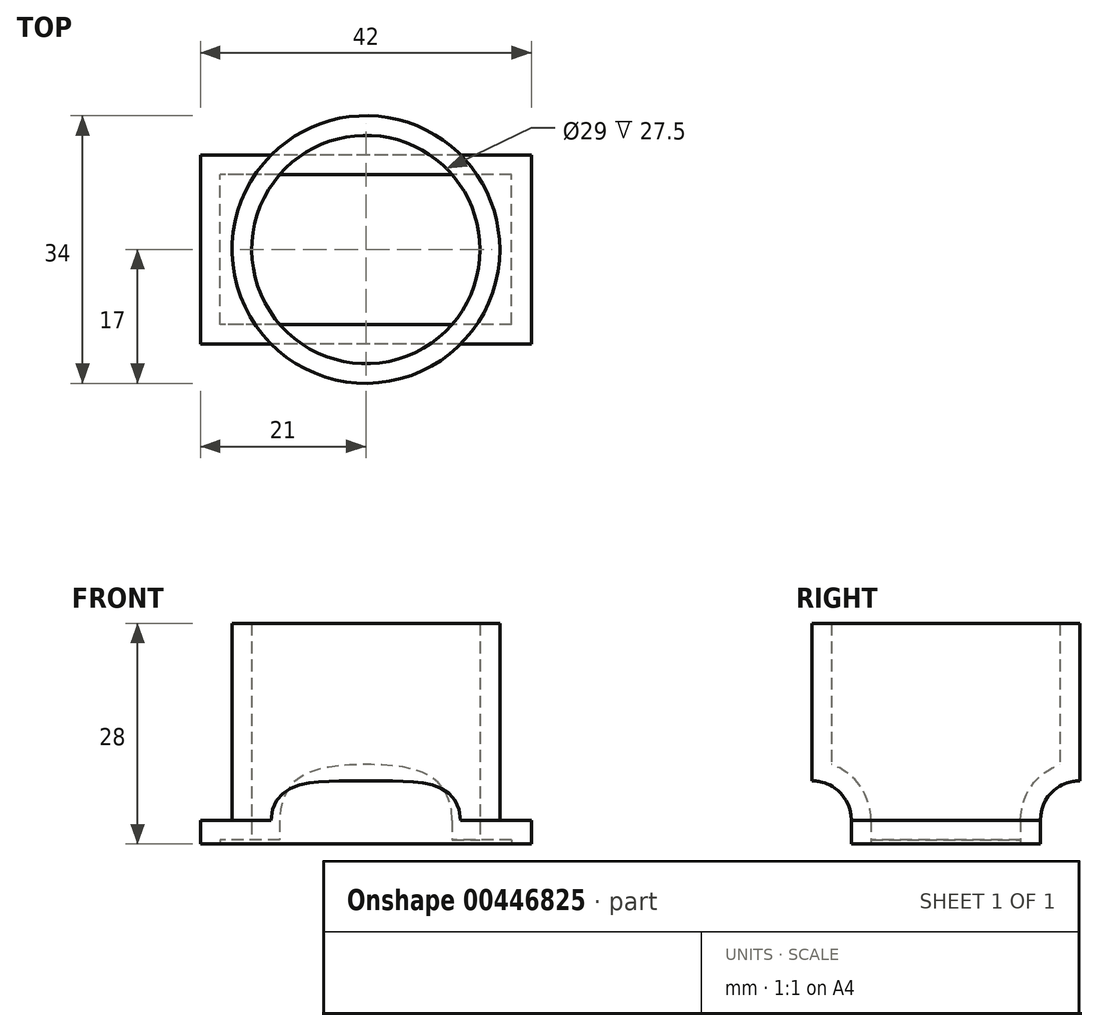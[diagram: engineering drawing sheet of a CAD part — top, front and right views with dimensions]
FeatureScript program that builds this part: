
annotation { "Feature Type Name" : "Feature", "Feature Type Description" : "" }
export const myFeature = defineFeature(function(context is Context, id is Id, definition is map)
    precondition{}
    {
        {
            var Q0;
            Q0=qCreatedBy(makeId("Top.planeOp"),FACE);
            var sketch = newSketch(context, id + "F0", { "sketchPlane" : qUnion([Q0])});
            skLineSegment(sketch, "E0.bottom", {"start": v(21, -12) * mm, "end": v(-21, -12) * mm});
            skLineSegment(sketch, "E0.top", {"start": v(21, 12) * mm, "end": v(-21, 12) * mm});
            skLineSegment(sketch, "E0.left", {"start": v(21, -12) * mm, "end": v(21, 12) * mm});
            skLineSegment(sketch, "E0.right", {"start": v(-21, -12) * mm, "end": v(-21, 12) * mm});
            skPoint(sketch, "E0.middle", {"position": v(0, 0) * mm});
            skSolve(sketch);
        }
        {
            var Q0;
            Q0=makeQuery(id+"F0.imprint","IMPRINT",FACE,{"disambiguationData":[TD([[makeQuery(id+"F0.imprint","IMPRINT",EDGE,{"derivedFrom":sQuery(id+"F0.wireOp",EDGE,"E0.bottom")}),-1.0]])]});
            extrude(context, id + "F1", {"entities" : qUnion([Q0]), "depth" : 3 * mm});
        }
        {
            var Q0;
            Q0=makeQuery(id+"F1.opExtrude","CAP_FACE",FACE,{"disambiguationData":[OSD([sQuery(id+"F0.wireOp",EDGE,"E0.bottom"),sQuery(id+"F0.wireOp",EDGE,"E0.top"),sQuery(id+"F0.wireOp",EDGE,"E0.left"),sQuery(id+"F0.wireOp",EDGE,"E0.right")])],"isStart":false});
            var sketch = newSketch(context, id + "F2", { "sketchPlane" : qUnion([Q0])});
            skCircle(sketch, "E1", {"center": v(0, 0) * mm, "radius": 17 * mm});
            skSolve(sketch);
        }
        {
            var Q0;
            {var subQ0=sQuery(id+"F2.wireOp",EDGE,"E1");var subQ1=makeQuery(id+"F1.opExtrude","CAP_EDGE",EDGE,{"disambiguationData":[OSD([sQuery(id+"F0.wireOp",EDGE,"E0.top")])],"isStart":false});var subQ2=makeQuery(id+"F2.imprint","INTERSECT",VERTEX,{"disambiguationData":[OD(0.0)],"derivedFrom":[subQ1,subQ0]});Q0=makeQuery(id+"F2.imprint","IMPRINT",FACE,{"disambiguationData":[TD([[makeQuery(id+"F2.imprint","IMPRINT",EDGE,{"disambiguationData":[TD([[subQ2,-1.0]])],"derivedFrom":subQ0}),1.0]])]});}
            var Q1;
            {var subQ0=sQuery(id+"F2.wireOp",EDGE,"E1");var subQ1=makeQuery(id+"F1.opExtrude","CAP_EDGE",EDGE,{"disambiguationData":[OSD([sQuery(id+"F0.wireOp",EDGE,"E0.top")])],"isStart":false});var subQ2=makeQuery(id+"F2.imprint","INTERSECT",VERTEX,{"disambiguationData":[OD(0.0)],"derivedFrom":[subQ1,subQ0]});Q1=makeQuery(id+"F2.imprint","IMPRINT",FACE,{"disambiguationData":[TD([[makeQuery(id+"F2.imprint","IMPRINT",EDGE,{"disambiguationData":[TD([[subQ2,1.0]])],"derivedFrom":subQ0}),1.0]])]});}
            var Q2;
            {var subQ0=sQuery(id+"F2.wireOp",EDGE,"E1");var subQ1=makeQuery(id+"F1.opExtrude","CAP_EDGE",EDGE,{"disambiguationData":[OSD([sQuery(id+"F0.wireOp",EDGE,"E0.bottom")])],"isStart":false});var subQ2=makeQuery(id+"F2.imprint","INTERSECT",VERTEX,{"disambiguationData":[OD(0.0)],"derivedFrom":[subQ1,subQ0]});Q2=makeQuery(id+"F2.imprint","IMPRINT",FACE,{"disambiguationData":[TD([[makeQuery(id+"F2.imprint","IMPRINT",EDGE,{"disambiguationData":[TD([[subQ2,-1.0]])],"derivedFrom":subQ0}),1.0]])]});}
            extrude(context, id + "F3", {"entities" : qUnion([Q0, Q1, Q2]), "operationType" : NewBodyOperationType.ADD, "depth" : 25 * mm});
        }
        {
            var Q0;
            {var subQ0=sQuery(id+"F0.wireOp",EDGE,"E0.top");var subQ1=sQuery(id+"F2.wireOp",EDGE,"E1");Q0=makeQuery(id+"F3.boolean.opBoolean","SPLIT",FACE,{"disambiguationData":[TD([makeQuery(id+"F1.opExtrude","SWEPT_FACE",FACE,{"disambiguationData":[OSD([subQ0])]})])],"derivedFrom":makeQuery(id+"F3.opExtrude","CAP_FACE",FACE,{"disambiguationData":[OSD([subQ1])],"isStart":true})});}
            var Q1;
            {var subQ0=sQuery(id+"F0.wireOp",EDGE,"E0.bottom");var subQ1=sQuery(id+"F2.wireOp",EDGE,"E1");Q1=makeQuery(id+"F3.boolean.opBoolean","SPLIT",FACE,{"disambiguationData":[TD([makeQuery(id+"F1.opExtrude","SWEPT_FACE",FACE,{"disambiguationData":[OSD([subQ0])]})])],"derivedFrom":makeQuery(id+"F3.opExtrude","CAP_FACE",FACE,{"disambiguationData":[OSD([subQ1])],"isStart":true})});}
            extrude(context, id + "F4", {"entities" : qUnion([Q0, Q1]), "operationType" : NewBodyOperationType.REMOVE, "oppositeDirection" : true, "depth" : 5 * mm});
        }
        {
            var Q0;
            Q0=makeQuery(id+"F4.boolean.opBoolean","COPY",EDGE,{"derivedFrom":makeQuery(id+"F4.opExtrude","CAP_EDGE",EDGE,{"disambiguationData":[OSD([sQuery(id+"F0.wireOp",EDGE,"E0.top")])],"isStart":false})});
            var Q1;
            Q1=makeQuery(id+"F4.boolean.opBoolean","COPY",EDGE,{"derivedFrom":makeQuery(id+"F4.opExtrude","CAP_EDGE",EDGE,{"disambiguationData":[OSD([sQuery(id+"F0.wireOp",EDGE,"E0.bottom")])],"isStart":false})});
            fillet(context, id + "F5", {"entities" : qUnion([Q0, Q1]), "radius" : 5 * mm, "tangentPropagation" : true, "allowEdgeOverflow" : false});
        }
        {
            var Q0;
            Q0=makeQuery(id+"F1.opExtrude","CAP_FACE",FACE,{"disambiguationData":[OSD([sQuery(id+"F0.wireOp",EDGE,"E0.bottom"),sQuery(id+"F0.wireOp",EDGE,"E0.top"),sQuery(id+"F0.wireOp",EDGE,"E0.left"),sQuery(id+"F0.wireOp",EDGE,"E0.right")])],"isStart":true});
            var Q1;
            Q1=makeQuery(id+"F3.opExtrude","CAP_FACE",FACE,{"disambiguationData":[OSD([sQuery(id+"F2.wireOp",EDGE,"E1")])],"isStart":false});
            shell(context, id + "F6", {"entities" : qUnion([Q0, Q1]), "thickness" : 2.5 * mm});
        }
    });
